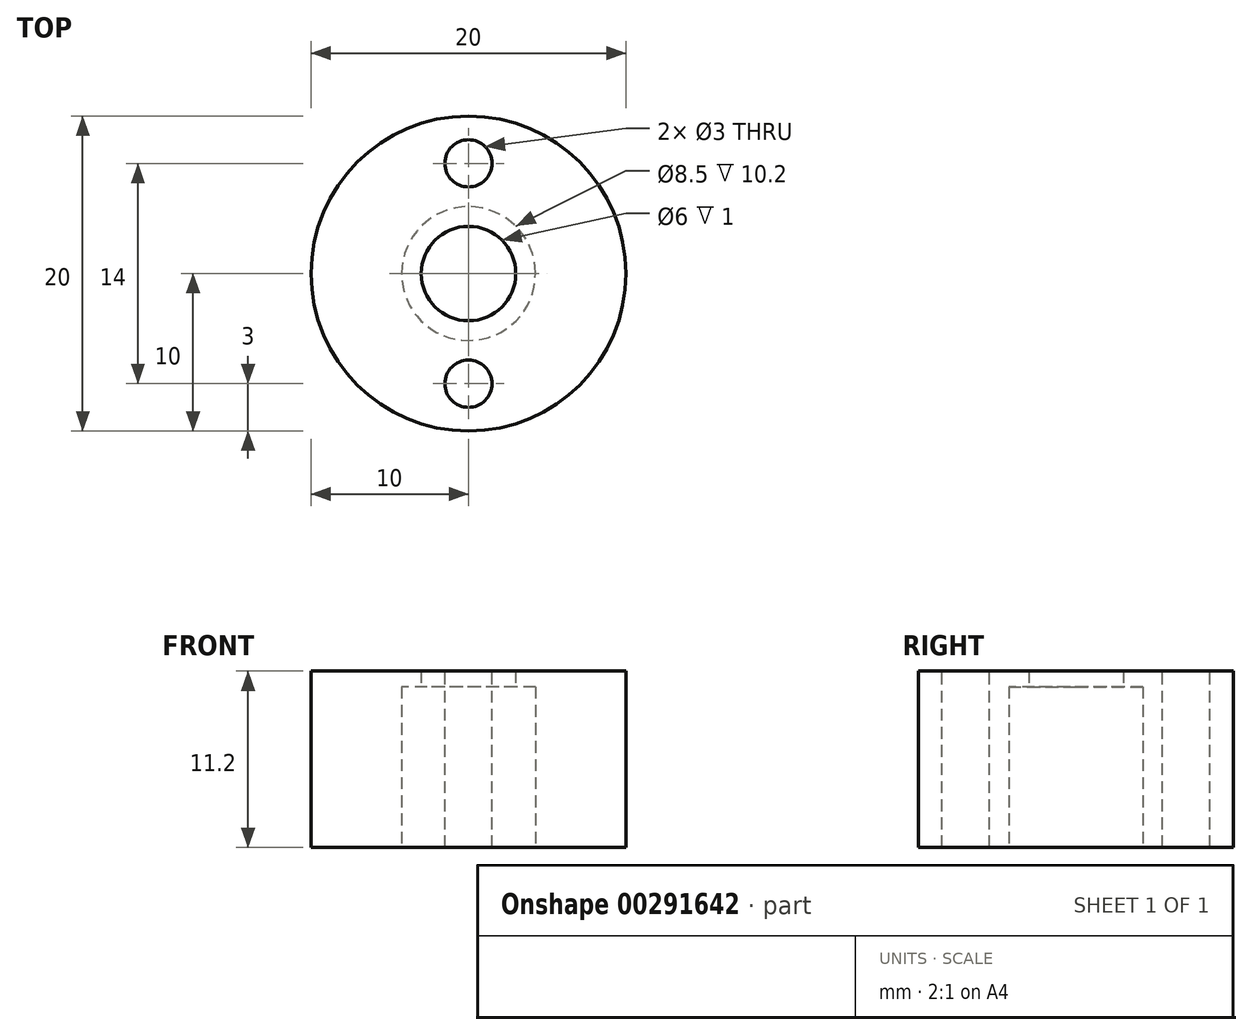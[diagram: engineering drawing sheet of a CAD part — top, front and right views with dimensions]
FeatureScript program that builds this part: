
annotation { "Feature Type Name" : "Feature", "Feature Type Description" : "" }
export const myFeature = defineFeature(function(context is Context, id is Id, definition is map)
    precondition{}
    {
        {
            var Q0;
            Q0=qCreatedBy(makeId("Top.planeOp"),FACE);
            var sketch = newSketch(context, id + "F0", { "sketchPlane" : qUnion([Q0])});
            skCircle(sketch, "E0", {"center": v(0, 0) * mm, "radius": 10 * mm});
            skCircle(sketch, "E1", {"center": v(0, 0) * mm, "radius": 4.25 * mm});
            skSolve(sketch);
        }
        {
            var Q0;
            Q0 = qSketchRegion(id + "F0", true);
            extrude(context, id + "F1", {"entities" : qUnion([Q0]), "depth" : 10.2 * mm});
        }
        {
            var Q0;
            Q0=makeQuery(id+"F1.opExtrude","CAP_FACE",FACE,{"disambiguationData":[OSD([sQuery(id+"F0.wireOp",EDGE,"E0"),sQuery(id+"F0.wireOp",EDGE,"E1")])],"isStart":false});
            cPlane(context, id + "F2", {"entities" : qUnion([Q0]), "cplaneType" : CPlaneType.OFFSET, "offset" : 0 * mm, "width" : 152.4 * mm, "height" : 152.4 * mm});
        }
        {
            var Q0;
            Q0=qCreatedBy(id+"F2.planeOp",FACE);
            var sketch = newSketch(context, id + "F3", { "sketchPlane" : qUnion([Q0])});
            skCircle(sketch, "E2", {"center": v(0, 0) * mm, "radius": 10 * mm});
            skCircle(sketch, "E3", {"center": v(0, 0) * mm, "radius": 3 * mm});
            skSolve(sketch);
        }
        {
            var Q0;
            Q0=makeQuery(id+"F3.imprint","IMPRINT",FACE,{"disambiguationData":[TD([[makeQuery(id+"F3.imprint","IMPRINT",EDGE,{"derivedFrom":sQuery(id+"F3.wireOp",EDGE,"E2")}),1.0]])]});
            extrude(context, id + "F4", {"entities" : qUnion([Q0]), "operationType" : NewBodyOperationType.ADD, "depth" : 1 * mm, "offsetDistance" : 25.4 * mm});
        }
        {
            var Q0;
            Q0=makeQuery(id+"F4.opExtrude","CAP_FACE",FACE,{"disambiguationData":[OSD([sQuery(id+"F3.wireOp",EDGE,"E2"),sQuery(id+"F3.wireOp",EDGE,"E3")])],"isStart":false});
            cPlane(context, id + "F5", {"entities" : qUnion([Q0]), "cplaneType" : CPlaneType.OFFSET, "offset" : 0 * mm, "width" : 152.4 * mm, "height" : 152.4 * mm});
        }
        {
            var Q0;
            Q0=qCreatedBy(id+"F5.planeOp",FACE);
            var sketch = newSketch(context, id + "F6", { "sketchPlane" : qUnion([Q0])});
            skLineSegment(sketch, "E4", {"start": v(0, -12.06) * mm, "end": v(0, 12.12) * mm});
            skCircle(sketch, "E5", {"center": v(0, -7) * mm, "radius": 1.5 * mm});
            skLineSegment(sketch, "E6", {"start": v(-8.73, 0) * mm, "end": v(11.46, 0) * mm});
            skCircle(sketch, "E7.MirrorC", {"center": v(0, 7) * mm, "radius": 1.5 * mm});
            skSolve(sketch);
        }
        {
            var Q0;
            Q0 = qSketchRegion(id + "F6", true);
            extrude(context, id + "F7", {"entities" : qUnion([Q0]), "operationType" : NewBodyOperationType.REMOVE, "oppositeDirection" : true, "depth" : 15 * mm});
        }
    });
